# Revit family: FP_Revit_18_CMO-24SS-3Y_Microwave_w_30in_Trimkit_90000928A
name_source: partatom
category: Specialty Equipment
revit_build: Autodesk Revit 2018 (Build: 20170223_1515(x64)
units: mm (PartAtom-declared; Revit-internal decimal feet)

## family parameters
Always vertical = Yes
Cut with Voids When Loaded = Yes
OmniClass Number = 23.40.40.14.17.31
OmniClass Title = Small Specialized Cooking Equipment
Part Type = Normal
Room Calculation Point = No
Round Connector Dimension = Use Diameter
Shared = No
Work Plane-Based = No

## types (1)
- FP_Revit_18_CMO-24SS-3Y_Microwave_w_30in_Trimkit_90000928A
    Cavity - Depth = 508 mm
    Cavity - Height = 487 mm  [stored 1.59777 ft]
    Cavity - Width = 654 mm  [stored 2.14567 ft]
    Chassis - Depth = 480 mm
    Chassis - Height = 487 mm  [stored 1.59777 ft]
    Chassis - Width = 654 mm  [stored 2.14567 ft]
    Connector Description - Electrical = 120 V, 60 Hz, 15 A
    Description = CMO-24SS-3Y Microwave + CMOTTK-30SS Trimkit
    Manufacturer = Fisher & Paykel Appliances
    Material - Body = Fisher & Paykel - Grey
    Material - Front = Fisher & Paykel - Stainless Steel
    Material - Glass = Fisher & Paykel - Glass, Black
    Model = CMO-24SS-3Y + CMOTTK-30SS
    Product - Depth = 518 mm  [stored 1.69948 ft]
    Product - Height = 521 mm  [stored 1.70932 ft]
    Product - Width = 754 mm  [stored 2.47375 ft]
    URL = www.fisherpaykel.com
    Visibility - Clearance Required = Yes

note: [stored X ft] marks values corroborated as IEEE doubles in the binary element streams (Revit-internal decimal feet)

## geometry (parser evidence)
native form markers: Sweep x6
no freeform markers — native parametric forms only
